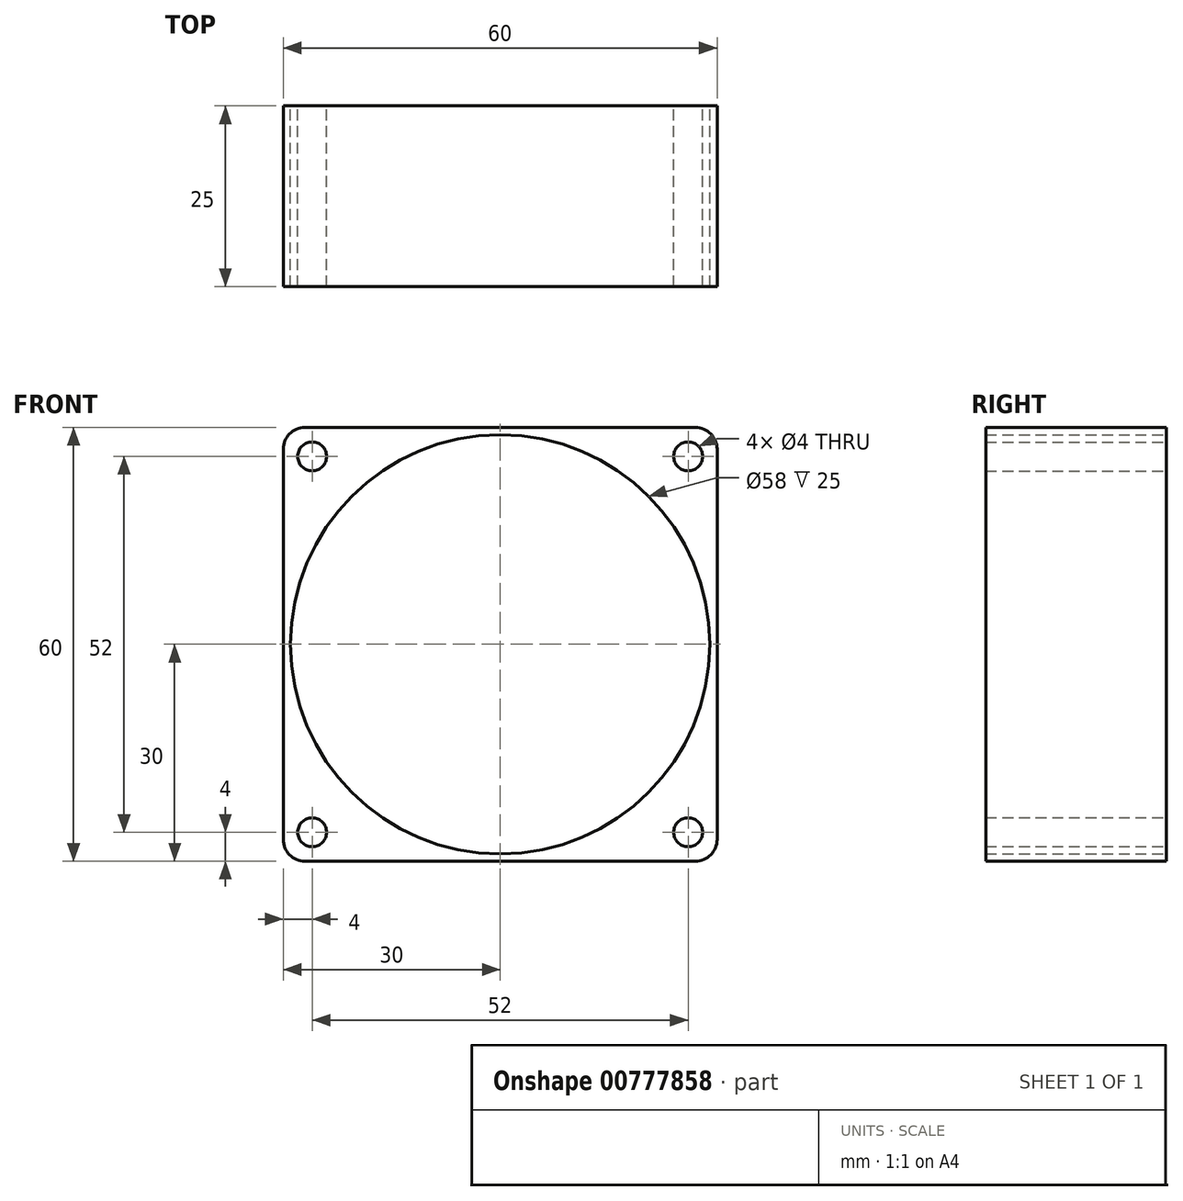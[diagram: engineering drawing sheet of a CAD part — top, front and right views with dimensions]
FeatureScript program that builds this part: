
annotation { "Feature Type Name" : "Feature", "Feature Type Description" : "" }
export const myFeature = defineFeature(function(context is Context, id is Id, definition is map)
    precondition{}
    {
        {
            var Q0;
            Q0=qCreatedBy(makeId("Front.planeOp"),FACE);
            var sketch = newSketch(context, id + "F0", { "sketchPlane" : qUnion([Q0])});
            skLineSegment(sketch, "E0.bottom", {"start": v(3, 0) * mm, "end": v(57, 0) * mm});
            skLineSegment(sketch, "E0.top", {"start": v(3, 60) * mm, "end": v(57, 60) * mm});
            skLineSegment(sketch, "E0.left", {"start": v(0, 3) * mm, "end": v(0, 57) * mm});
            skLineSegment(sketch, "E0.right", {"start": v(60, 3) * mm, "end": v(60, 57) * mm});
            skPoint(sketch, "E1.visualSharp", {"position": v(60, 60) * mm});
            skArc(sketch, "E1.filletArc", {"start": v(60, 57) * mm, "mid": v(59.12, 59.12) * mm, "end": v(57, 60) * mm});
            skPoint(sketch, "E2.visualSharp", {"position": v(60, 0) * mm});
            skArc(sketch, "E2.filletArc", {"start": v(57, 0) * mm, "mid": v(59.12, 0.88) * mm, "end": v(60, 3) * mm});
            skPoint(sketch, "E3.visualSharp", {"position": v(0, 0) * mm});
            skArc(sketch, "E3.filletArc", {"start": v(0, 3) * mm, "mid": v(0.88, 0.88) * mm, "end": v(3, 0) * mm});
            skPoint(sketch, "E4.visualSharp", {"position": v(0, 60) * mm});
            skArc(sketch, "E4.filletArc", {"start": v(3, 60) * mm, "mid": v(0.88, 59.12) * mm, "end": v(0, 57) * mm});
            skCircle(sketch, "E5", {"center": v(30, 30) * mm, "radius": 29 * mm});
            skPoint(sketch, "E5.centerSnap0", {"position": v(0, 30) * mm});
            skPoint(sketch, "E5.centerSnap1", {"position": v(30, 60) * mm});
            skCircle(sketch, "E6", {"center": v(4, 56) * mm, "radius": 2 * mm});
            skCircle(sketch, "E7", {"center": v(56, 56) * mm, "radius": 2 * mm});
            skCircle(sketch, "E8", {"center": v(4, 4) * mm, "radius": 2 * mm});
            skCircle(sketch, "E9", {"center": v(56, 4) * mm, "radius": 2 * mm});
            skSolve(sketch);
        }
        {
            var Q0;
            Q0 = qSketchRegion(id + "F0", true);
            extrude(context, id + "F1", {"entities" : qUnion([Q0]), "depth" : 25 * mm, "offsetDistance" : 25 * mm});
        }
        {
            var Q0;
            {var subQ0=sQuery(id+"F0.wireOp",EDGE,"E5");var subQ1=makeQuery(id+"F0.imprint","INTERSECT",VERTEX,{"derivedFrom":[sQuery(id+"F0.wireOp",EDGE,"E0.left"),subQ0]});Q0=makeQuery(id+"F0.imprint","IMPRINT",FACE,{"disambiguationData":[TD([[makeQuery(id+"F0.imprint","IMPRINT",EDGE,{"disambiguationData":[TD([[subQ1,1.0]])],"derivedFrom":subQ0}),1.0]])]});}
            extrude(context, id + "F2", {"entities" : qUnion([Q0]), "operationType" : NewBodyOperationType.REMOVE, "depth" : 25 * mm, "offsetDistance" : 25 * mm});
        }
    });
